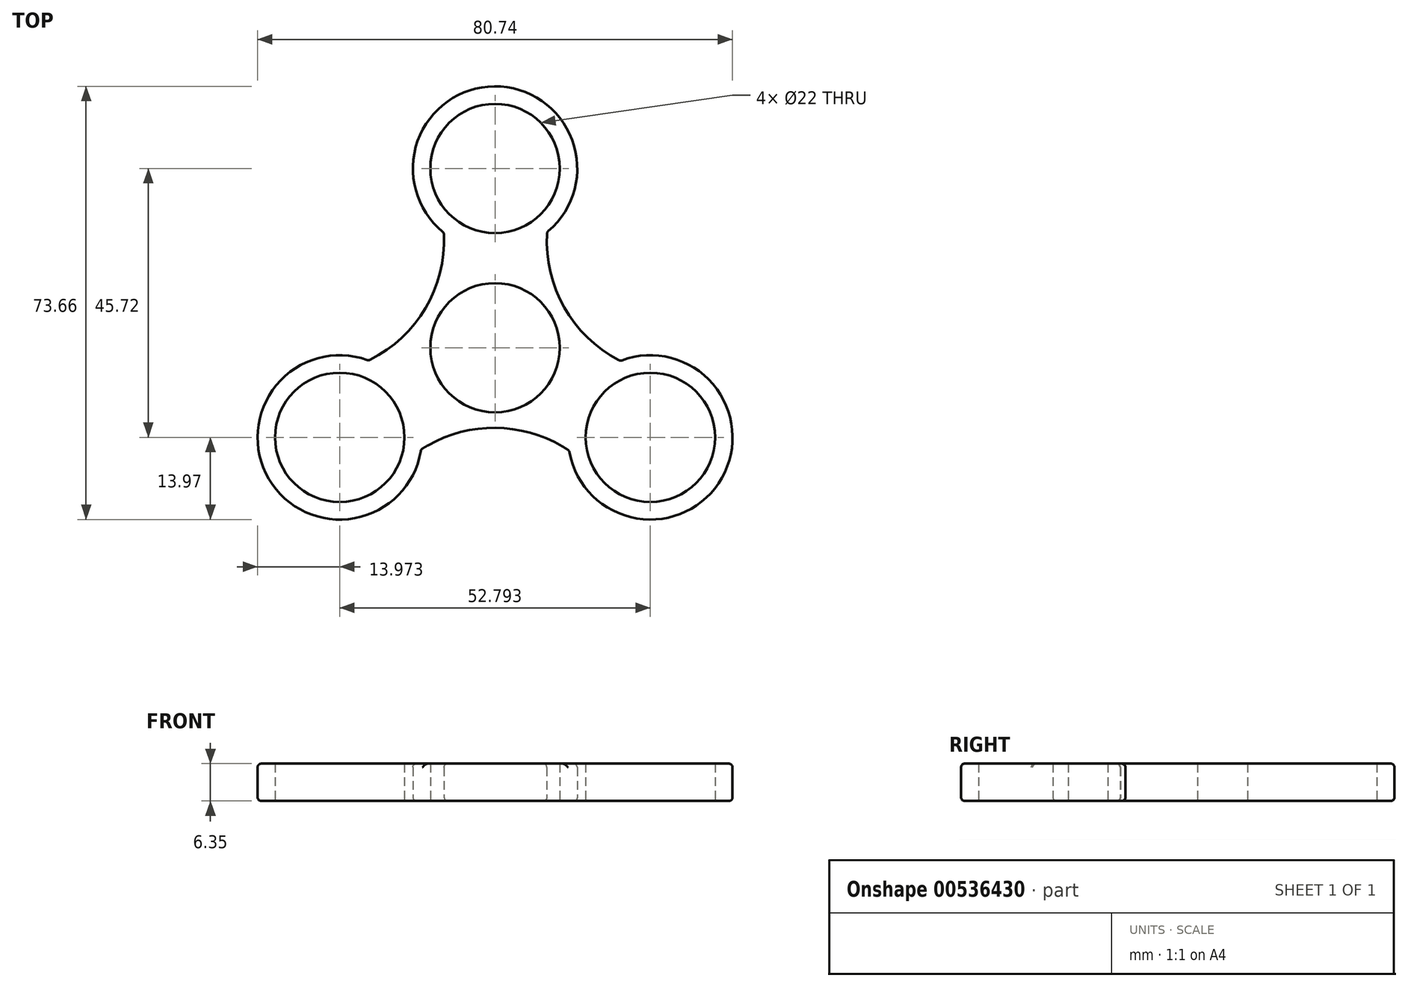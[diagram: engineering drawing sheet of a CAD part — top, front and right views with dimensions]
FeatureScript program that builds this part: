
annotation { "Feature Type Name" : "Feature", "Feature Type Description" : "" }
export const myFeature = defineFeature(function(context is Context, id is Id, definition is map)
    precondition{}
    {
        {
            var Q0;
            Q0=qCreatedBy(makeId("Top.planeOp"),FACE);
            var sketch = newSketch(context, id + "F0", { "sketchPlane" : qUnion([Q0])});
            skCircle(sketch, "E0", {"center": v(0, 0) * mm, "radius": 44.45 * mm});
            skCircle(sketch, "E1", {"center": v(0, 0) * mm, "radius": 11 * mm});
            skLineSegment(sketch, "E2", {"start": v(0, 0) * mm, "end": v(0, 30.48) * mm});
            skCircle(sketch, "E3", {"center": v(0, 30.48) * mm, "radius": 11 * mm});
            skCircle(sketch, "E4", {"center": v(0, 30.48) * mm, "radius": 13.97 * mm});
            skCircle(sketch, "E5.1.0", {"center": v(-26.4, -15.24) * mm, "radius": 13.97 * mm});
            skCircle(sketch, "E5.1.1", {"center": v(-26.4, -15.24) * mm, "radius": 11 * mm});
            skCircle(sketch, "E5.2.0", {"center": v(26.4, -15.24) * mm, "radius": 13.97 * mm});
            skCircle(sketch, "E5.2.1", {"center": v(26.4, -15.24) * mm, "radius": 11 * mm});
            skCircle(sketch, "E6", {"center": v(0, 0) * mm, "radius": 13.97 * mm});
            skArc(sketch, "E7", {"start": v(12.61, -17.51) * mm, "mid": v(0.05, -13.62) * mm, "end": v(-12.58, -17.3) * mm});
            skArc(sketch, "E8.1.0", {"start": v(8.86, 19.68) * mm, "mid": v(11.77, 6.85) * mm, "end": v(21.27, -2.25) * mm});
            skArc(sketch, "E8.2.0", {"start": v(-21.47, -2.17) * mm, "mid": v(-11.82, 6.76) * mm, "end": v(-8.69, 19.54) * mm});
            skSolve(sketch);
        }
        {
            var Q0;
            Q0=makeQuery(id+"F0.imprint","IMPRINT",FACE,{"disambiguationData":[TD([[makeQuery(id+"F0.imprint","IMPRINT",EDGE,{"derivedFrom":sQuery(id+"F0.wireOp",EDGE,"E3")}),-1.0]])]});
            var Q1;
            Q1=makeQuery(id+"F0.imprint","IMPRINT",FACE,{"disambiguationData":[TD([[makeQuery(id+"F0.imprint","IMPRINT",EDGE,{"derivedFrom":sQuery(id+"F0.wireOp",EDGE,"E5.2.0")}),1.0]])]});
            var Q2;
            Q2=makeQuery(id+"F0.imprint","IMPRINT",FACE,{"disambiguationData":[TD([[makeQuery(id+"F0.imprint","IMPRINT",EDGE,{"derivedFrom":sQuery(id+"F0.wireOp",EDGE,"E5.1.0")}),1.0]])]});
            var Q3;
            Q3=makeQuery(id+"F0.imprint","IMPRINT",FACE,{"disambiguationData":[TD([[makeQuery(id+"F0.imprint","IMPRINT",EDGE,{"derivedFrom":sQuery(id+"F0.wireOp",EDGE,"E1")}),-1.0]])]});
            var Q4;
            {var subQ0=sQuery(id+"F0.wireOp",EDGE,"E4");var subQ1=sQuery(id+"F0.wireOp",EDGE,"E2");var subQ2=makeQuery(id+"F0.imprint","INTERSECT",VERTEX,{"derivedFrom":[subQ1,subQ0]});Q4=makeQuery(id+"F0.imprint","IMPRINT",FACE,{"disambiguationData":[TD([[makeQuery(id+"F0.imprint","IMPRINT",EDGE,{"disambiguationData":[TD([[subQ2,1.0]])],"derivedFrom":subQ1}),1.0]])]});}
            var Q5;
            {var subQ0=sQuery(id+"F0.wireOp",EDGE,"E4");var subQ1=sQuery(id+"F0.wireOp",EDGE,"E2");var subQ2=makeQuery(id+"F0.imprint","INTERSECT",VERTEX,{"derivedFrom":[subQ1,subQ0]});Q5=makeQuery(id+"F0.imprint","IMPRINT",FACE,{"disambiguationData":[TD([[makeQuery(id+"F0.imprint","IMPRINT",EDGE,{"disambiguationData":[TD([[subQ2,1.0]])],"derivedFrom":subQ1}),-1.0]])]});}
            var Q6;
            {var subQ0=sQuery(id+"F0.wireOp",EDGE,"E7");var subQ1=sQuery(id+"F0.wireOp",EDGE,"E5.2.0");var subQ2=makeQuery(id+"F0.imprint","INTERSECT",VERTEX,{"derivedFrom":[subQ1,subQ0]});Q6=makeQuery(id+"F0.imprint","IMPRINT",FACE,{"disambiguationData":[TD([[makeQuery(id+"F0.imprint","IMPRINT",EDGE,{"disambiguationData":[TD([[subQ2,1.0]])],"derivedFrom":subQ1}),-1.0]])]});}
            var Q7;
            {var subQ0=sQuery(id+"F0.wireOp",EDGE,"E7");var subQ1=sQuery(id+"F0.wireOp",EDGE,"E5.1.0");var subQ2=makeQuery(id+"F0.imprint","INTERSECT",VERTEX,{"derivedFrom":[subQ1,subQ0]});Q7=makeQuery(id+"F0.imprint","IMPRINT",FACE,{"disambiguationData":[TD([[makeQuery(id+"F0.imprint","IMPRINT",EDGE,{"disambiguationData":[TD([[subQ2,-1.0]])],"derivedFrom":subQ1}),-1.0]])]});}
            extrude(context, id + "F1", {"entities" : qUnion([Q0, Q1, Q2, Q3, Q4, Q5, Q6, Q7]), "depth" : 6.35 * mm, "offsetDistance" : 25.4 * mm});
        }
        {
            var Q0;
            Q0=makeQuery(id+"F1.opExtrude","CAP_EDGE",EDGE,{"disambiguationData":[OSD([sQuery(id+"F0.wireOp",EDGE,"E8.1.0")])],"isStart":false});
            var Q1;
            Q1=makeQuery(id+"F1.opExtrude","CAP_EDGE",EDGE,{"disambiguationData":[OSD([sQuery(id+"F0.wireOp",EDGE,"E8.2.0")])],"isStart":false});
            var Q2;
            Q2=makeQuery(id+"F1.opExtrude","CAP_EDGE",EDGE,{"disambiguationData":[OSD([sQuery(id+"F0.wireOp",EDGE,"E8.2.0")])],"isStart":true});
            var Q3;
            Q3=makeQuery(id+"F1.opExtrude","CAP_EDGE",EDGE,{"disambiguationData":[OSD([sQuery(id+"F0.wireOp",EDGE,"E8.1.0")])],"isStart":true});
            var Q4;
            Q4=makeQuery(id+"F1.opExtrude","CAP_EDGE",EDGE,{"disambiguationData":[OSD([sQuery(id+"F0.wireOp",EDGE,"E7")])],"isStart":true});
            var Q5;
            Q5=makeQuery(id+"F1.opExtrude","SWEPT_FACE",FACE,{"disambiguationData":[OSD([sQuery(id+"F0.wireOp",EDGE,"E4")])]});
            var Q6;
            Q6=makeQuery(id+"F1.opExtrude","SWEPT_FACE",FACE,{"disambiguationData":[OSD([sQuery(id+"F0.wireOp",EDGE,"E5.2.0")])]});
            var Q7;
            Q7=makeQuery(id+"F1.opExtrude","SWEPT_FACE",FACE,{"disambiguationData":[OSD([sQuery(id+"F0.wireOp",EDGE,"E5.1.0")])]});
            fillet(context, id + "F2", {"entities" : qUnion([Q0, Q1, Q2, Q3, Q4, Q5, Q6, Q7]), "radius" : 0.64 * mm, "tangentPropagation" : true, "allowEdgeOverflow" : false});
        }
    });
